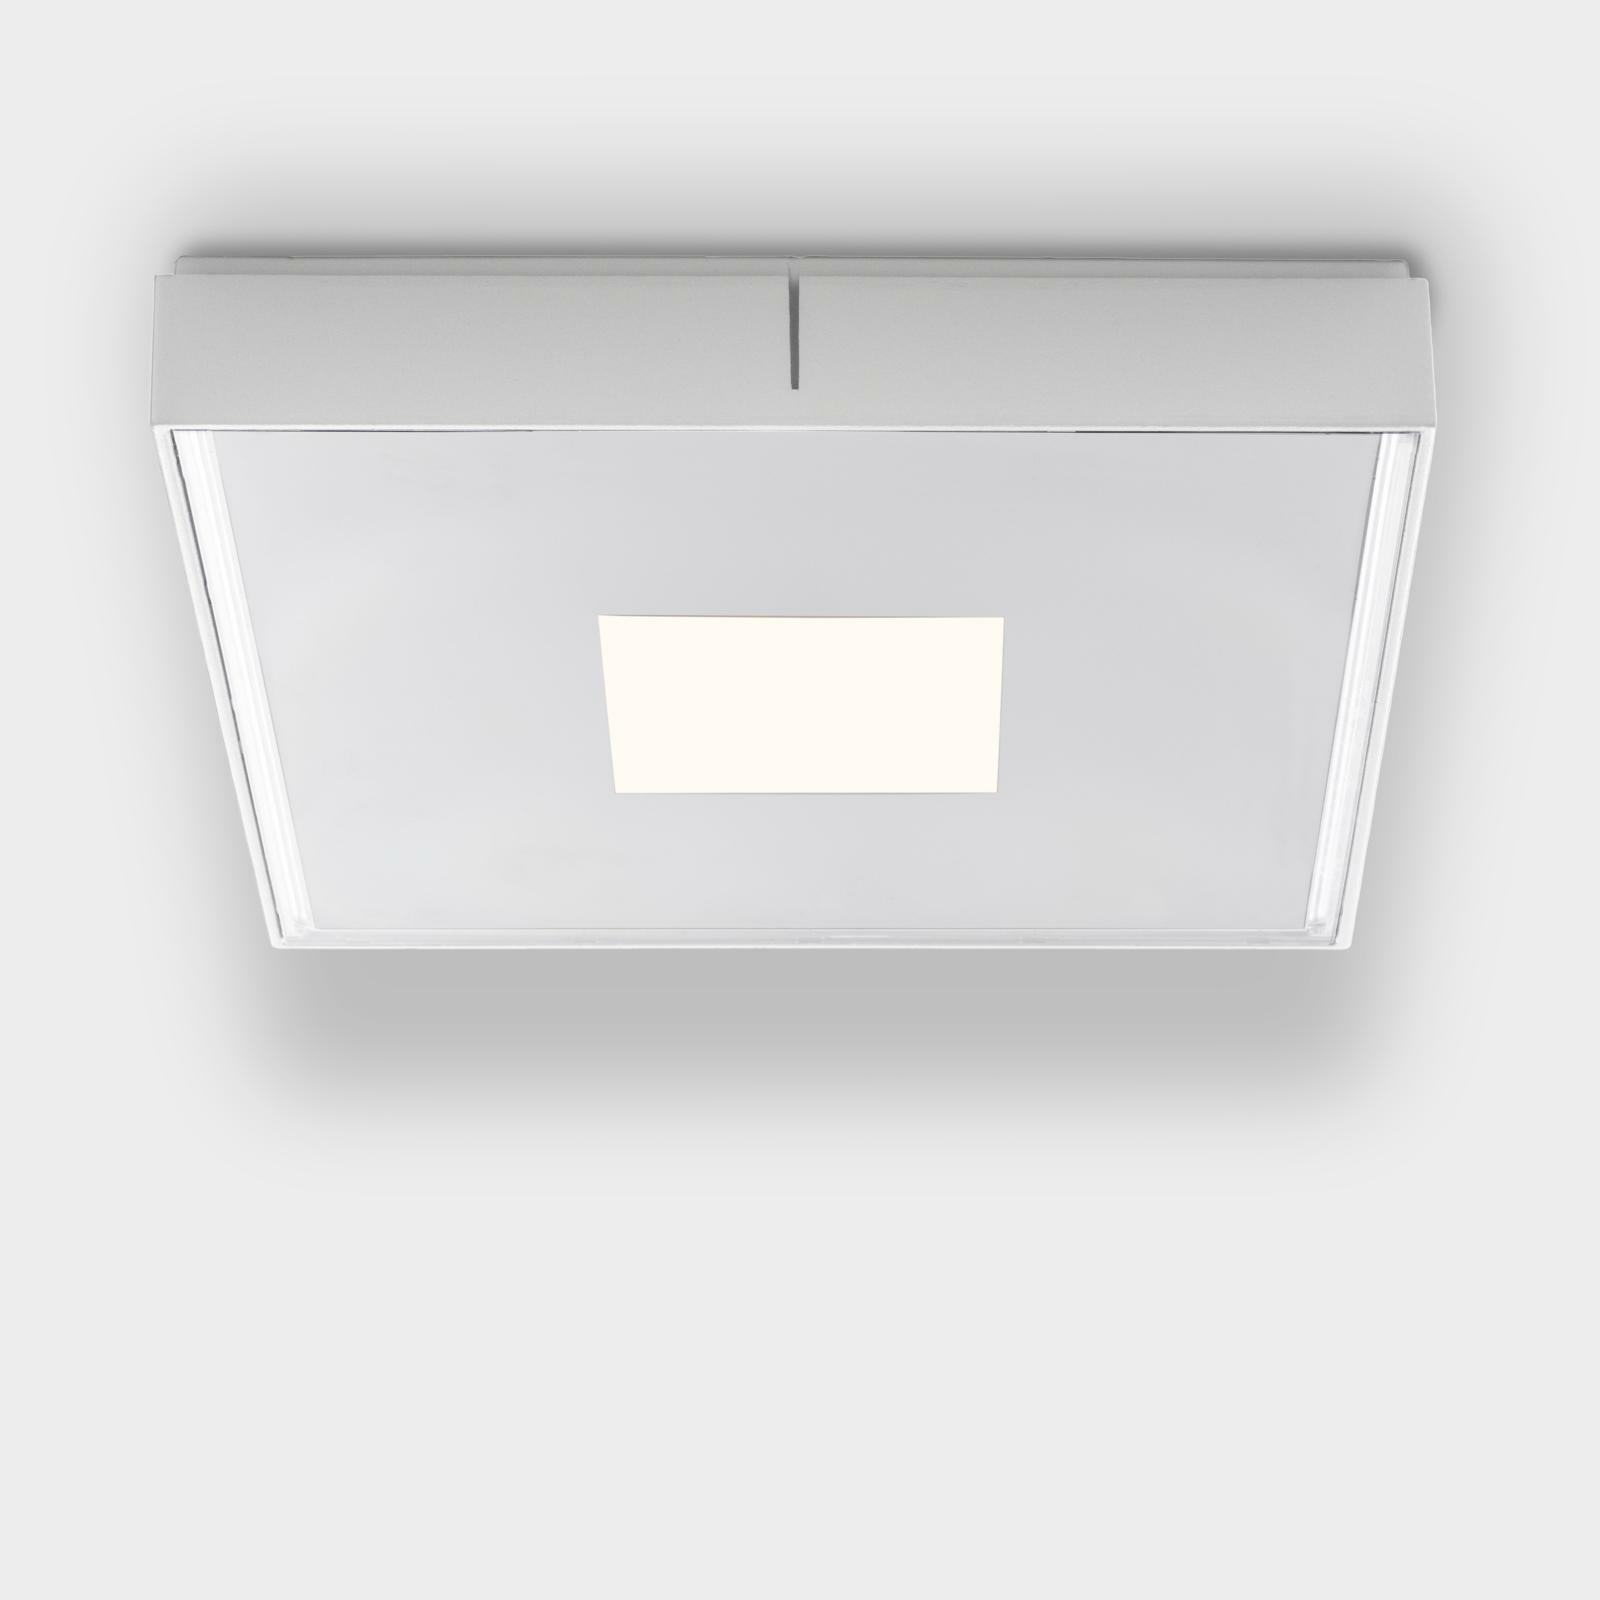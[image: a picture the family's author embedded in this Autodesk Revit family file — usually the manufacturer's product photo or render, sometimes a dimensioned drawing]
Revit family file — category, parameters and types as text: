
# Revit family: PN 230
name_source: partatom
category: Lighting Fixtures
units: mm (PartAtom-declared; Revit-internal decimal feet)

## family parameters
Cut with Voids When Loaded = No
Host = Face
Light Source = Yes
OmniClass Number = 23.80.70.11
OmniClass Title = Luminaries for Internal Lighting
Part Type = Normal
Room Calculation Point = No
Round Connector Dimension = Use Diameter
Shared = No

## types (2) — shared parameters
Beam angle (°) = 110°
CRI L'indice di Resa Cromatica = 85
Color Filter = 16777215
Description = La plafoniera per esterni  PN 230 coniuga l'elementare figura geometrica del quadrato con la tecnologia LED COB di ultima generazione, che ha permesso di ridurre notevolmente le dimensioni del prodotto, garantendo un'estrema sottigliezza. Il design lineare consente al prodotto di integrarsi in atri, ingressi, balconi, portici, aree residenziali e spazi a verde in generale.
Il corpo in pressofusione di alluminio è progettato per garantire la dissipazione passiva del calore generato dal LED.
Lo schermo  frontale, senza viti a vista, è in materiale termoplastico trasparente ad alta resistenza, UV protetto.
La sorgente luminosa è schermata da un diffusore in policarbonato opale ad alta capacità diffondente.
Dimming Lamp Color Temperature Shift = <None>
Effective Intensity (lm) = 2040
Glass material = White Traslucido
Lamp = LED 2400lm 18W 3000K CRI85
Larghezza = 230 mm
Manufacturer = ARIA
Model = 14400
Photometric Web File = 1440 _ PN 230 LED 18W 2400 lm.IES
Tilt Angle = 90.00°
Type Comments = Ceiling outdoor light
URL = https://www.aria.lighting
Wattage Comments = 18

## per-type parameters (varying)
| type | Body material | Codice | Type Image |
| PN 230 WHITE | White Powder Coated Aluminium | 144004 | PN 230 WHITE.jpg |
| PN 230 BLACK | Black Powder Coated Aluminium | 144001 | PN 230 BLACK.jpg |

## geometry (parser evidence)
native form markers: Sweep x3
no freeform markers — native parametric forms only
